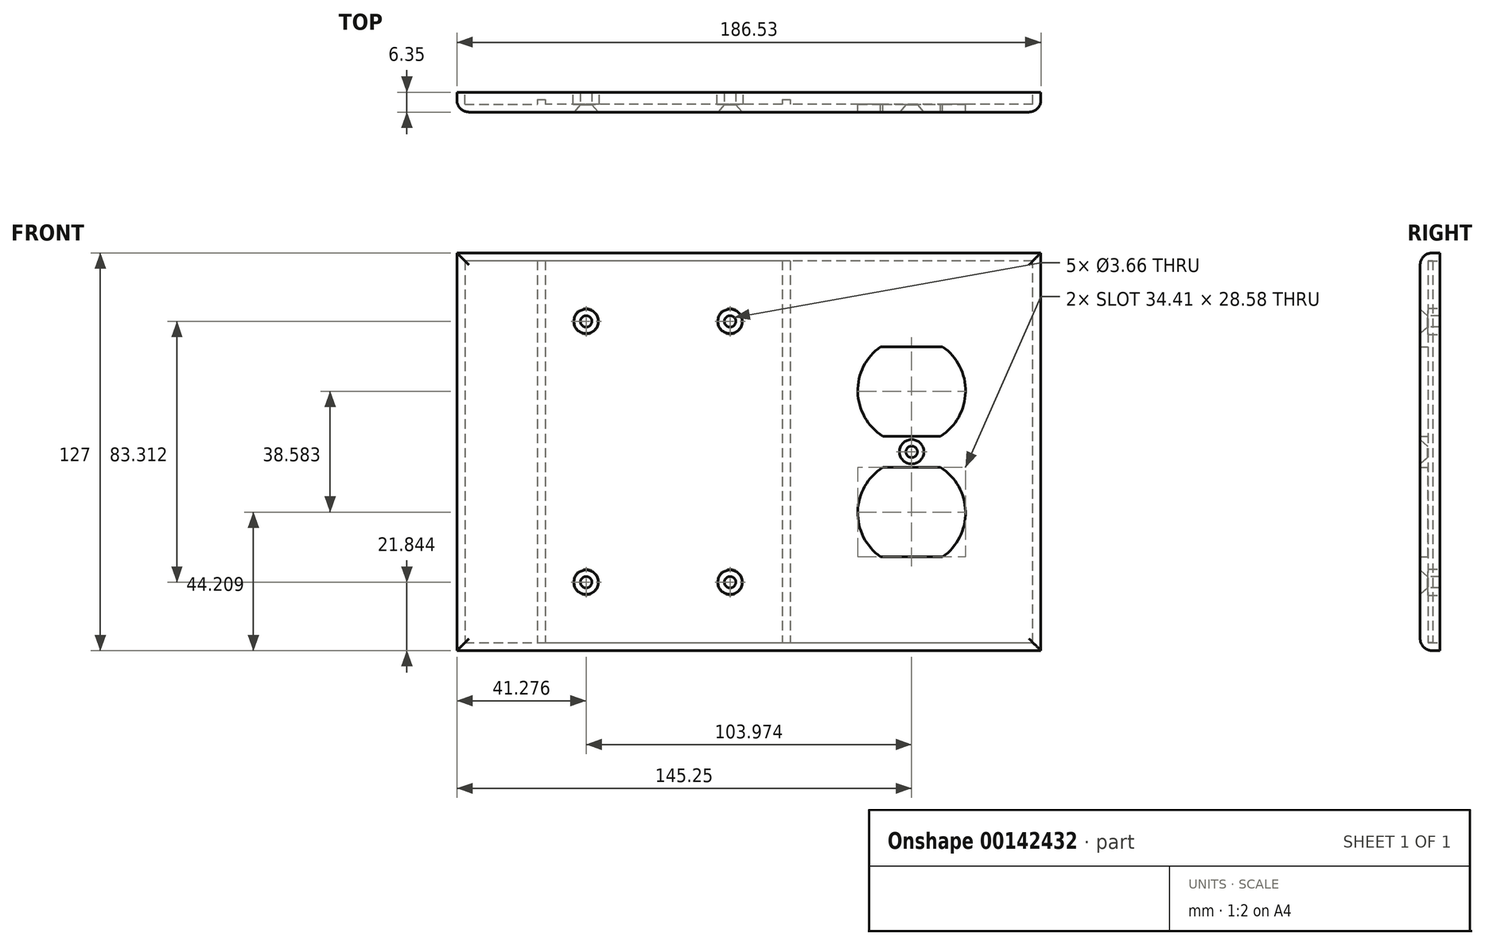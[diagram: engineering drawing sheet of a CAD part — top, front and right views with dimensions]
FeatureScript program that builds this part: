
annotation { "Feature Type Name" : "Feature", "Feature Type Description" : "" }
export const myFeature = defineFeature(function(context is Context, id is Id, definition is map)
    precondition{}
    {
        {
            var Q0;
            Q0=qCreatedBy(makeId("Front.planeOp"),FACE);
            var sketch = newSketch(context, id + "F0", { "sketchPlane" : qUnion([Q0])});
            skLineSegment(sketch, "E0.left", {"start": v(41.28, -63.5) * mm, "end": v(41.27, 63.5) * mm});
            skPoint(sketch, "E0.middle", {"position": v(0, 0) * mm});
            skLineSegment(sketch, "E1", {"start": v(-9.26, 5) * mm, "end": v(9.26, 5) * mm});
            skLineSegment(sketch, "E2.0", {"start": v(-9.9, 33.58) * mm, "end": v(9.9, 33.58) * mm});
            skCircle(sketch, "E3", {"center": v(0, 0) * mm, "radius": 1.66 * mm});
            skArc(sketch, "E4", {"start": v(-9.9, 33.58) * mm, "mid": v(-17.2, 19.12) * mm, "end": v(-9.26, 5) * mm});
            skArc(sketch, "E5.trimOffspring", {"start": v(9.26, 5) * mm, "mid": v(17.2, 19.12) * mm, "end": v(9.9, 33.58) * mm});
            skLineSegment(sketch, "E6", {"start": v(-29.44, 0) * mm, "end": v(83.32, 0) * mm, "construction": true});
            skLineSegment(sketch, "E7.MirrorCS", {"start": v(-9.9, -33.58) * mm, "end": v(9.9, -33.58) * mm});
            skArc(sketch, "E8.MirrorCS", {"start": v(-9.9, -33.58) * mm, "mid": v(-17.2, -19.12) * mm, "end": v(-9.26, -5) * mm});
            skArc(sketch, "E9.MirrorCS", {"start": v(9.26, -5) * mm, "mid": v(17.2, -19.12) * mm, "end": v(9.9, -33.58) * mm});
            skLineSegment(sketch, "E10.MirrorCS", {"start": v(-9.26, -5) * mm, "end": v(9.26, -5) * mm});
            skLineSegment(sketch, "E11", {"start": v(41.27, 63.5) * mm, "end": v(-145.25, 63.5) * mm});
            skLineSegment(sketch, "E12", {"start": v(-145.25, 63.5) * mm, "end": v(-145.25, -63.5) * mm});
            skLineSegment(sketch, "E13", {"start": v(-145.25, -63.5) * mm, "end": v(41.28, -63.5) * mm});
            skCircle(sketch, "E14", {"center": v(-103.97, 41.66) * mm, "radius": 1.66 * mm});
            skCircle(sketch, "E15", {"center": v(-58, 41.66) * mm, "radius": 1.66 * mm});
            skCircle(sketch, "E16.MirrorC", {"center": v(-58, -41.66) * mm, "radius": 1.66 * mm});
            skCircle(sketch, "E17.MirrorC", {"center": v(-103.97, -41.66) * mm, "radius": 1.66 * mm});
            skSolve(sketch);
        }
        {
            var Q0;
            Q0 = qSketchRegion(id + "F0", true);
            extrude(context, id + "F1", {"entities" : qUnion([Q0]), "depth" : 6.35 * mm});
        }
        {
            var Q0;
            Q0=makeQuery(id+"F1.opExtrude","CAP_FACE",FACE,{"disambiguationData":[OSD([sQuery(id+"F0.wireOp",EDGE,"E0.left"),sQuery(id+"F0.wireOp",EDGE,"E1"),sQuery(id+"F0.wireOp",EDGE,"E2.0"),sQuery(id+"F0.wireOp",EDGE,"E3"),sQuery(id+"F0.wireOp",EDGE,"E4"),sQuery(id+"F0.wireOp",EDGE,"E5.trimOffspring"),sQuery(id+"F0.wireOp",EDGE,"E7.MirrorCS"),sQuery(id+"F0.wireOp",EDGE,"E8.MirrorCS"),sQuery(id+"F0.wireOp",EDGE,"E9.MirrorCS"),sQuery(id+"F0.wireOp",EDGE,"E10.MirrorCS"),sQuery(id+"F0.wireOp",EDGE,"E11"),sQuery(id+"F0.wireOp",EDGE,"E12"),sQuery(id+"F0.wireOp",EDGE,"E13")])],"isStart":true});
            shell(context, id + "F2", {"entities" : qUnion([Q0]), "thickness" : 2.54 * mm});
        }
        {
            var Q0;
            {var subQ0=sQuery(id+"F0.wireOp",EDGE,"E17.MirrorC");var subQ1=sQuery(id+"F0.wireOp",EDGE,"E16.MirrorC");var subQ2=sQuery(id+"F0.wireOp",EDGE,"E15");var subQ3=sQuery(id+"F0.wireOp",EDGE,"E14");var subQ4=sQuery(id+"F0.wireOp",EDGE,"E13");var subQ5=sQuery(id+"F0.wireOp",EDGE,"E12");var subQ6=sQuery(id+"F0.wireOp",EDGE,"E11");var subQ7=sQuery(id+"F0.wireOp",EDGE,"E10.MirrorCS");var subQ8=sQuery(id+"F0.wireOp",EDGE,"E9.MirrorCS");var subQ9=sQuery(id+"F0.wireOp",EDGE,"E8.MirrorCS");var subQ10=sQuery(id+"F0.wireOp",EDGE,"E7.MirrorCS");var subQ11=sQuery(id+"F0.wireOp",EDGE,"E5.trimOffspring");var subQ12=sQuery(id+"F0.wireOp",EDGE,"E4");var subQ13=sQuery(id+"F0.wireOp",EDGE,"E3");var subQ14=sQuery(id+"F0.wireOp",EDGE,"E2.0");var subQ15=sQuery(id+"F0.wireOp",EDGE,"E1");var subQ16=sQuery(id+"F0.wireOp",EDGE,"E0.left");Q0=makeQuery(id+"F2.opShell","OFFSET_FACE",FACE,{"disambiguationData":[OSD([subQ16,subQ15,subQ14,subQ13,subQ12,subQ11,subQ10,subQ9,subQ8,subQ7,subQ6,subQ5,subQ4,subQ3,subQ2,subQ1,subQ0]),TDD([makeQuery(id+"F1.opExtrude","CAP_FACE",FACE,{"disambiguationData":[OSD([subQ16,subQ15,subQ14,subQ13,subQ12,subQ11,subQ10,subQ9,subQ8,subQ7,subQ6,subQ5,subQ4,subQ3,subQ2,subQ1,subQ0])],"isStart":true})]),OD(4.0)]});}
            var Q1;
            {var subQ0=sQuery(id+"F0.wireOp",EDGE,"E13");var subQ1=sQuery(id+"F0.wireOp",EDGE,"E12");var subQ2=sQuery(id+"F0.wireOp",EDGE,"E11");var subQ3=sQuery(id+"F0.wireOp",EDGE,"E10.MirrorCS");var subQ4=sQuery(id+"F0.wireOp",EDGE,"E9.MirrorCS");var subQ5=sQuery(id+"F0.wireOp",EDGE,"E8.MirrorCS");var subQ6=sQuery(id+"F0.wireOp",EDGE,"E7.MirrorCS");var subQ7=sQuery(id+"F0.wireOp",EDGE,"E5.trimOffspring");var subQ8=sQuery(id+"F0.wireOp",EDGE,"E4");var subQ9=sQuery(id+"F0.wireOp",EDGE,"E3");var subQ10=sQuery(id+"F0.wireOp",EDGE,"E2.0");var subQ11=sQuery(id+"F0.wireOp",EDGE,"E1");var subQ12=sQuery(id+"F0.wireOp",EDGE,"E0.left");Q1=makeQuery(id+"F2.opShell","OFFSET_FACE",FACE,{"disambiguationData":[OSD([subQ12,subQ11,subQ10,subQ9,subQ8,subQ7,subQ6,subQ5,subQ4,subQ3,subQ2,subQ1,subQ0]),TDD([makeQuery(id+"F1.opExtrude","CAP_FACE",FACE,{"disambiguationData":[OSD([subQ12,subQ11,subQ10,subQ9,subQ8,subQ7,subQ6,subQ5,subQ4,subQ3,subQ2,subQ1,subQ0])],"isStart":false})])]});}
            var Q2;
            {var subQ0=sQuery(id+"F0.wireOp",EDGE,"E13");var subQ1=sQuery(id+"F0.wireOp",EDGE,"E12");var subQ2=sQuery(id+"F0.wireOp",EDGE,"E11");var subQ3=sQuery(id+"F0.wireOp",EDGE,"E10.MirrorCS");var subQ4=sQuery(id+"F0.wireOp",EDGE,"E9.MirrorCS");var subQ5=sQuery(id+"F0.wireOp",EDGE,"E8.MirrorCS");var subQ6=sQuery(id+"F0.wireOp",EDGE,"E7.MirrorCS");var subQ7=sQuery(id+"F0.wireOp",EDGE,"E5.trimOffspring");var subQ8=sQuery(id+"F0.wireOp",EDGE,"E4");var subQ9=sQuery(id+"F0.wireOp",EDGE,"E3");var subQ10=sQuery(id+"F0.wireOp",EDGE,"E2.0");var subQ11=sQuery(id+"F0.wireOp",EDGE,"E1");var subQ12=sQuery(id+"F0.wireOp",EDGE,"E0.left");Q2=makeQuery(id+"F2.opShell","OFFSET_FACE",FACE,{"disambiguationData":[OSD([subQ12,subQ11,subQ10,subQ9,subQ8,subQ7,subQ6,subQ5,subQ4,subQ3,subQ2,subQ1,subQ0]),TDD([makeQuery(id+"F1.opExtrude","CAP_FACE",FACE,{"disambiguationData":[OSD([subQ12,subQ11,subQ10,subQ9,subQ8,subQ7,subQ6,subQ5,subQ4,subQ3,subQ2,subQ1,subQ0])],"isStart":false})])]});}
            extrude(context, id + "F3", {"entities" : qUnion([Q0]), "operationType" : NewBodyOperationType.REMOVE, "endBound" : BoundingType.UP_TO_SURFACE, "oppositeDirection" : true, "endBoundEntityFace" : qUnion([Q1]), "depth" : 25.4 * mm});
        }
        {
            var Q0;
            Q0=makeQuery(id+"F1.opExtrude","CAP_EDGE",EDGE,{"disambiguationData":[OSD([sQuery(id+"F0.wireOp",EDGE,"E12")])],"isStart":false});
            var Q1;
            Q1=makeQuery(id+"F1.opExtrude","CAP_EDGE",EDGE,{"disambiguationData":[OSD([sQuery(id+"F0.wireOp",EDGE,"E11")])],"isStart":false});
            var Q2;
            Q2=makeQuery(id+"F1.opExtrude","CAP_EDGE",EDGE,{"disambiguationData":[OSD([sQuery(id+"F0.wireOp",EDGE,"E0.left")])],"isStart":false});
            var Q3;
            Q3=makeQuery(id+"F1.opExtrude","CAP_EDGE",EDGE,{"disambiguationData":[OSD([sQuery(id+"F0.wireOp",EDGE,"E13")])],"isStart":false});
            fillet(context, id + "F4", {"entities" : qUnion([Q0, Q1, Q2, Q3]), "radius" : 3.8 * mm, "tangentPropagation" : true, "allowEdgeOverflow" : false});
        }
        {
            var Q0;
            Q0=qCreatedBy(makeId("Front.planeOp"),FACE);
            var sketch = newSketch(context, id + "F5", { "sketchPlane" : qUnion([Q0])});
            skLineSegment(sketch, "E18", {"start": v(-25.51, 60.03) * mm, "end": v(-25.51, -64.13) * mm, "construction": true});
            skSolve(sketch);
        }
        {
            var Q0;
            Q0=sQuery(id+"F5.wireOp",EDGE,"E18");
            cPlane(context, id + "F6", {"entities" : qUnion([Q0]), "cplaneType" : CPlaneType.LINE_ANGLE, "offset" : 25.4 * mm, "angle" : 0 * degree, "flipAlignment" : true, "width" : 152.4 * mm, "height" : 152.4 * mm});
        }
        {
            var Q0;
            Q0=makeQuery(id+"F1.opExtrude","CAP_FACE",FACE,{"disambiguationData":[OSD([sQuery(id+"F0.wireOp",EDGE,"E0.left"),sQuery(id+"F0.wireOp",EDGE,"E1"),sQuery(id+"F0.wireOp",EDGE,"E2.0"),sQuery(id+"F0.wireOp",EDGE,"E3"),sQuery(id+"F0.wireOp",EDGE,"E4"),sQuery(id+"F0.wireOp",EDGE,"E5.trimOffspring"),sQuery(id+"F0.wireOp",EDGE,"E7.MirrorCS"),sQuery(id+"F0.wireOp",EDGE,"E8.MirrorCS"),sQuery(id+"F0.wireOp",EDGE,"E9.MirrorCS"),sQuery(id+"F0.wireOp",EDGE,"E10.MirrorCS"),sQuery(id+"F0.wireOp",EDGE,"E11"),sQuery(id+"F0.wireOp",EDGE,"E12"),sQuery(id+"F0.wireOp",EDGE,"E13"),sQuery(id+"F0.wireOp",EDGE,"E14"),sQuery(id+"F0.wireOp",EDGE,"E15"),sQuery(id+"F0.wireOp",EDGE,"E16.MirrorC"),sQuery(id+"F0.wireOp",EDGE,"E17.MirrorC")])],"isStart":false});
            cPlane(context, id + "F7", {"entities" : qUnion([Q0]), "cplaneType" : CPlaneType.OFFSET, "offset" : 0 * mm, "width" : 152.4 * mm, "height" : 152.4 * mm});
        }
        {
            var Q0;
            Q0=qCreatedBy(id+"F7.planeOp",FACE);
            var sketch = newSketch(context, id + "F8", { "sketchPlane" : qUnion([Q0])});
            skCircle(sketch, "E19.0", {"center": v(-103.97, 41.66) * mm, "radius": 1.9 * mm});
            skCircle(sketch, "E20.0", {"center": v(-58, 41.66) * mm, "radius": 1.66 * mm});
            skCircle(sketch, "E21.0", {"center": v(-58, -41.66) * mm, "radius": 1.66 * mm});
            skCircle(sketch, "E22.0", {"center": v(-103.97, -41.66) * mm, "radius": 1.66 * mm});
            skCircle(sketch, "E23.0", {"center": v(0, 0) * mm, "radius": 1.66 * mm});
            skSolve(sketch);
        }
        {
            var Q0;
            Q0=sQuery(id+"F8.wireOp",VERTEX,"E19.0.center");
            var Q1;
            Q1=sQuery(id+"F8.wireOp",VERTEX,"E22.0.center");
            var Q2;
            Q2=sQuery(id+"F8.wireOp",VERTEX,"E21.0.center");
            var Q3;
            Q3=sQuery(id+"F8.wireOp",VERTEX,"E20.0.center");
            var Q4;
            Q4=sQuery(id+"F8.wireOp",VERTEX,"E23.0.center");
            var Q5;
            Q5=makeQuery(id+"F1.opExtrude","SWEPT_BODY",BODY,{"disambiguationData":[OSD([sQuery(id+"F0.wireOp",EDGE,"E0.left"),sQuery(id+"F0.wireOp",EDGE,"E1"),sQuery(id+"F0.wireOp",EDGE,"E2.0"),sQuery(id+"F0.wireOp",EDGE,"E3"),sQuery(id+"F0.wireOp",EDGE,"E4"),sQuery(id+"F0.wireOp",EDGE,"E5.trimOffspring"),sQuery(id+"F0.wireOp",EDGE,"E7.MirrorCS"),sQuery(id+"F0.wireOp",EDGE,"E8.MirrorCS"),sQuery(id+"F0.wireOp",EDGE,"E9.MirrorCS"),sQuery(id+"F0.wireOp",EDGE,"E10.MirrorCS"),sQuery(id+"F0.wireOp",EDGE,"E11"),sQuery(id+"F0.wireOp",EDGE,"E12"),sQuery(id+"F0.wireOp",EDGE,"E13"),sQuery(id+"F0.wireOp",EDGE,"E14"),sQuery(id+"F0.wireOp",EDGE,"E15"),sQuery(id+"F0.wireOp",EDGE,"E16.MirrorC"),sQuery(id+"F0.wireOp",EDGE,"E17.MirrorC")])]});
            hole(context, id + "F9", {"style" : HoleStyle.C_SINK, "endStyle" : HoleEndStyle.THROUGH, "standardTappedOrClearance" : lookupTablePath({ "standard" : "ANSI", "fit" : "Close", "size" : "#6", "type" : "Clearance" }), "standardBlindInLast" : lookupTablePath({ "fit" : "Close", "standard" : "ANSI", "size" : "#6", "type" : "Clearance" }), "holeDiameter" : 3.66 * mm, "cSinkDiameter" : 7.8 * mm, "cSinkAngle" : 82 * degree, "locations" : qUnion([Q0, Q1, Q2, Q3, Q4]), "scope" : qUnion([Q5]), "isTappedThrough" : true});
        }
        {
            var Q0;
            {var subQ0=sQuery(id+"F0.wireOp",EDGE,"E17.MirrorC");var subQ1=sQuery(id+"F0.wireOp",EDGE,"E16.MirrorC");var subQ2=sQuery(id+"F0.wireOp",EDGE,"E15");var subQ3=sQuery(id+"F0.wireOp",EDGE,"E14");var subQ4=sQuery(id+"F0.wireOp",EDGE,"E13");var subQ5=sQuery(id+"F0.wireOp",EDGE,"E12");var subQ6=sQuery(id+"F0.wireOp",EDGE,"E11");var subQ7=sQuery(id+"F0.wireOp",EDGE,"E10.MirrorCS");var subQ8=sQuery(id+"F0.wireOp",EDGE,"E9.MirrorCS");var subQ9=sQuery(id+"F0.wireOp",EDGE,"E8.MirrorCS");var subQ10=sQuery(id+"F0.wireOp",EDGE,"E7.MirrorCS");var subQ11=sQuery(id+"F0.wireOp",EDGE,"E5.trimOffspring");var subQ12=sQuery(id+"F0.wireOp",EDGE,"E4");var subQ13=sQuery(id+"F0.wireOp",EDGE,"E3");var subQ14=sQuery(id+"F0.wireOp",EDGE,"E2.0");var subQ15=sQuery(id+"F0.wireOp",EDGE,"E1");var subQ16=sQuery(id+"F0.wireOp",EDGE,"E0.left");Q0=makeQuery(id+"F3.boolean.opBoolean","MERGE",FACE,{"derivedFrom":[makeQuery(id+"F2.opShell","OFFSET_FACE",FACE,{"disambiguationData":[OSD([subQ16,subQ15,subQ14,subQ13,subQ12,subQ11,subQ10,subQ9,subQ8,subQ7,subQ6,subQ5,subQ4,subQ3,subQ2,subQ1,subQ0]),TDD([makeQuery(id+"F1.opExtrude","CAP_FACE",FACE,{"disambiguationData":[OSD([subQ16,subQ15,subQ14,subQ13,subQ12,subQ11,subQ10,subQ9,subQ8,subQ7,subQ6,subQ5,subQ4,subQ3,subQ2,subQ1,subQ0])],"isStart":false})])]}),makeQuery(id+"F3.opExtrude","CAP_FACE",FACE,{"disambiguationData":[OSD([subQ16,subQ15,subQ14,subQ13,subQ12,subQ11,subQ10,subQ9,subQ8,subQ7,subQ6,subQ5,subQ4,subQ3,subQ2,subQ1,subQ0])],"isStart":false})]});}
            var sketch = newSketch(context, id + "F10", { "sketchPlane" : qUnion([Q0])});
            skCircle(sketch, "E24.0", {"center": v(0, 0) * mm, "radius": 1.83 * mm});
            skLineSegment(sketch, "E25.0", {"start": v(-38.74, -60.96) * mm, "end": v(-38.73, 60.96) * mm});
            skLineSegment(sketch, "E26", {"start": v(38.73, 60.96) * mm, "end": v(38.74, -60.96) * mm});
            skLineSegment(sketch, "E27.0", {"start": v(41.27, 60.96) * mm, "end": v(41.28, -60.96) * mm});
            skLineSegment(sketch, "E28", {"start": v(38.74, -60.96) * mm, "end": v(41.28, -60.96) * mm});
            skLineSegment(sketch, "E29", {"start": v(41.27, 60.96) * mm, "end": v(38.73, 60.96) * mm});
            skLineSegment(sketch, "E30", {"start": v(117.03, 60.96) * mm, "end": v(117.03, -60.96) * mm});
            skLineSegment(sketch, "E31.0", {"start": v(119.57, 60.96) * mm, "end": v(119.57, -60.96) * mm});
            skLineSegment(sketch, "E32", {"start": v(117.03, -60.96) * mm, "end": v(119.57, -60.96) * mm});
            skLineSegment(sketch, "E33", {"start": v(119.57, 60.96) * mm, "end": v(117.03, 60.96) * mm});
            skSolve(sketch);
        }
        {
            var Q0;
            Q0=makeQuery(id+"F10.imprint","IMPRINT",FACE,{"disambiguationData":[TD([[makeQuery(id+"F10.imprint","IMPRINT",EDGE,{"derivedFrom":sQuery(id+"F10.wireOp",EDGE,"E26")}),1.0]])]});
            var Q1;
            Q1=makeQuery(id+"F10.imprint","IMPRINT",FACE,{"disambiguationData":[TD([[makeQuery(id+"F10.imprint","IMPRINT",EDGE,{"derivedFrom":sQuery(id+"F10.wireOp",EDGE,"E30")}),1.0]])]});
            var Q2;
            Q2=makeQuery(id+"F1.opExtrude","CAP_FACE",FACE,{"disambiguationData":[OSD([sQuery(id+"F0.wireOp",EDGE,"E0.left"),sQuery(id+"F0.wireOp",EDGE,"E1"),sQuery(id+"F0.wireOp",EDGE,"E2.0"),sQuery(id+"F0.wireOp",EDGE,"E3"),sQuery(id+"F0.wireOp",EDGE,"E4"),sQuery(id+"F0.wireOp",EDGE,"E5.trimOffspring"),sQuery(id+"F0.wireOp",EDGE,"E7.MirrorCS"),sQuery(id+"F0.wireOp",EDGE,"E8.MirrorCS"),sQuery(id+"F0.wireOp",EDGE,"E9.MirrorCS"),sQuery(id+"F0.wireOp",EDGE,"E10.MirrorCS"),sQuery(id+"F0.wireOp",EDGE,"E11"),sQuery(id+"F0.wireOp",EDGE,"E12"),sQuery(id+"F0.wireOp",EDGE,"E13"),sQuery(id+"F0.wireOp",EDGE,"E14"),sQuery(id+"F0.wireOp",EDGE,"E15"),sQuery(id+"F0.wireOp",EDGE,"E16.MirrorC"),sQuery(id+"F0.wireOp",EDGE,"E17.MirrorC")])],"isStart":true});
            extrude(context, id + "F11", {"entities" : qUnion([Q0, Q1]), "operationType" : NewBodyOperationType.ADD, "endBoundEntityFace" : qUnion([Q2]), "depth" : 1.5 * mm});
        }
    });
